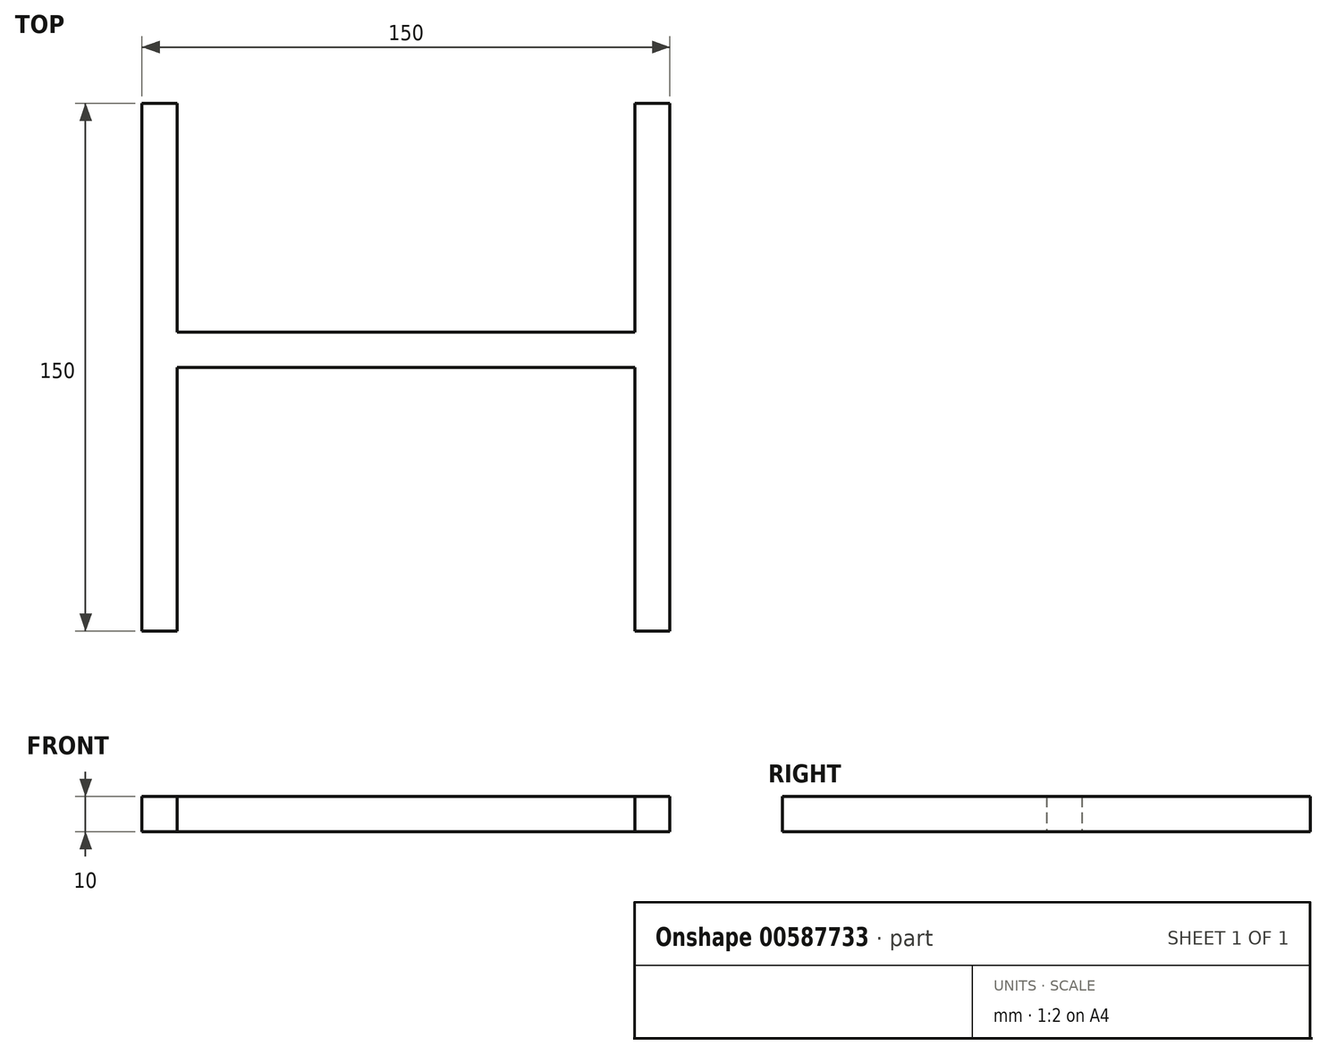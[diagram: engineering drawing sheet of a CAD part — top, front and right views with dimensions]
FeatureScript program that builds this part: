
annotation { "Feature Type Name" : "Feature", "Feature Type Description" : "" }
export const myFeature = defineFeature(function(context is Context, id is Id, definition is map)
    precondition{}
    {
        {
            var Q0;
            Q0=qCreatedBy(makeId("Top.planeOp"),FACE);
            var sketch = newSketch(context, id + "F0", { "sketchPlane" : qUnion([Q0])});
            skLineSegment(sketch, "E0.top", {"start": v(-65, -5) * mm, "end": v(65, -5) * mm});
            skPoint(sketch, "E0.middle", {"position": v(0, 0) * mm});
            skLineSegment(sketch, "E1.bottom", {"start": v(-75, -80) * mm, "end": v(-65, -80) * mm});
            skLineSegment(sketch, "E1.top", {"start": v(-75, 70) * mm, "end": v(-65, 70) * mm});
            skLineSegment(sketch, "E1.left", {"start": v(-75, -80) * mm, "end": v(-75, 70) * mm});
            skLineSegment(sketch, "E1.right", {"start": v(-65, -80) * mm, "end": v(-65, -5) * mm});
            skLineSegment(sketch, "E2.bottom", {"start": v(75, -80) * mm, "end": v(65, -80) * mm});
            skLineSegment(sketch, "E2.top", {"start": v(75, 70) * mm, "end": v(65, 70) * mm});
            skLineSegment(sketch, "E2.left", {"start": v(75, -80) * mm, "end": v(75, 70) * mm});
            skLineSegment(sketch, "E2.right", {"start": v(65, -80) * mm, "end": v(65, -5) * mm});
            skLineSegment(sketch, "E3.trimOffspring", {"start": v(-65, 5) * mm, "end": v(-65, 70) * mm});
            skLineSegment(sketch, "E4.trimOffspring", {"start": v(65, 5) * mm, "end": v(65, 70) * mm});
            skLineSegment(sketch, "E5", {"start": v(-65, 5) * mm, "end": v(65, 5) * mm});
            skSolve(sketch);
        }
        {
            var Q0;
            Q0=makeQuery(id+"F0.imprint","IMPRINT",FACE,{"disambiguationData":[TD([[makeQuery(id+"F0.imprint","IMPRINT",EDGE,{"derivedFrom":sQuery(id+"F0.wireOp",EDGE,"E0.top")}),1.0]])]});
            extrude(context, id + "F1", {"entities" : qUnion([Q0]), "endBound" : BoundingType.SYMMETRIC, "depth" : 10 * mm, "offsetDistance" : 25 * mm});
        }
    });
